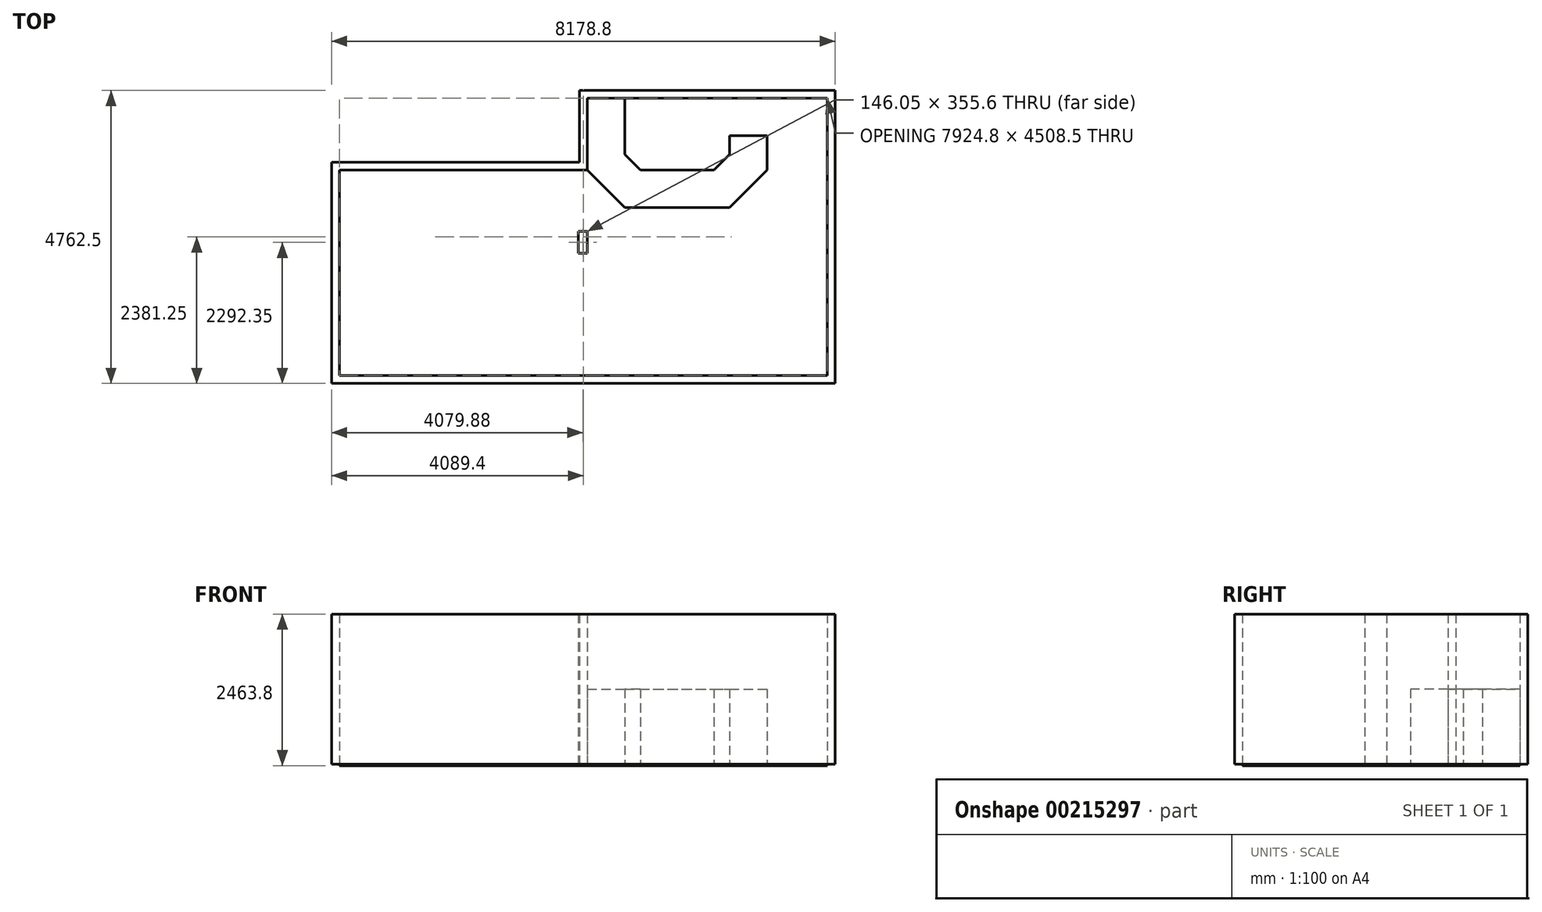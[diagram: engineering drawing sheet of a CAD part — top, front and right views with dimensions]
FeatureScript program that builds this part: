
annotation { "Feature Type Name" : "Feature", "Feature Type Description" : "" }
export const myFeature = defineFeature(function(context is Context, id is Id, definition is map)
    precondition{}
    {
        {
            var Q0;
            Q0=qCreatedBy(makeId("Top.planeOp"),FACE);
            var sketch = newSketch(context, id + "F0", { "sketchPlane" : qUnion([Q0])});
            skLineSegment(sketch, "E0.bottom", {"start": v(3962.4, 2254.25) * mm, "end": v(63.5, 2254.25) * mm});
            skLineSegment(sketch, "E0.top", {"start": v(3962.4, -2254.25) * mm, "end": v(-3962.4, -2254.25) * mm});
            skLineSegment(sketch, "E0.left", {"start": v(3962.4, 2254.25) * mm, "end": v(3962.4, -2254.25) * mm});
            skLineSegment(sketch, "E0.right", {"start": v(-3962.4, 1085.85) * mm, "end": v(-3962.4, -2254.25) * mm});
            skPoint(sketch, "E0.middle", {"position": v(0, 0) * mm});
            skLineSegment(sketch, "E1", {"start": v(63.5, 2254.25) * mm, "end": v(63.5, 1085.85) * mm});
            skLineSegment(sketch, "E2", {"start": v(63.5, 1085.85) * mm, "end": v(-3962.4, 1085.85) * mm});
            skLineSegment(sketch, "E3.bottom", {"start": v(63.5, 88.9) * mm, "end": v(-82.55, 88.9) * mm});
            skLineSegment(sketch, "E3.top", {"start": v(63.5, -266.7) * mm, "end": v(-82.55, -266.7) * mm});
            skLineSegment(sketch, "E3.left", {"start": v(63.5, 88.9) * mm, "end": v(63.5, -266.7) * mm});
            skLineSegment(sketch, "E3.right", {"start": v(-82.55, 88.9) * mm, "end": v(-82.55, -266.7) * mm});
            skPoint(sketch, "E4.orphan", {"position": v(-3962.4, 2254.25) * mm});
            skLineSegment(sketch, "E5", {"start": v(-63.5, 2381.25) * mm, "end": v(4089.4, 2381.25) * mm});
            skLineSegment(sketch, "E6", {"start": v(4089.4, 2381.25) * mm, "end": v(4089.4, -2381.25) * mm});
            skLineSegment(sketch, "E7", {"start": v(-4089.4, -2381.25) * mm, "end": v(4089.4, -2381.25) * mm});
            skLineSegment(sketch, "E8", {"start": v(-4089.4, -2381.25) * mm, "end": v(-4089.4, 1212.85) * mm});
            skLineSegment(sketch, "E9", {"start": v(-4089.4, 1212.85) * mm, "end": v(-63.5, 1212.85) * mm});
            skLineSegment(sketch, "E10", {"start": v(-63.5, 1212.85) * mm, "end": v(-63.5, 2381.25) * mm});
            skSolve(sketch);
        }
        {
            var Q0;
            Q0=makeQuery(id+"F0.imprint","IMPRINT",FACE,{"disambiguationData":[TD([[makeQuery(id+"F0.imprint","IMPRINT",EDGE,{"derivedFrom":sQuery(id+"F0.wireOp",EDGE,"E0.bottom")}),-1.0]])]});
            extrude(context, id + "F1", {"entities" : qUnion([Q0]), "depth" : 2438.4 * mm});
        }
        {
            var Q0;
            Q0=makeQuery(id+"F0.imprint","IMPRINT",FACE,{"disambiguationData":[TD([[makeQuery(id+"F0.imprint","IMPRINT",EDGE,{"derivedFrom":sQuery(id+"F0.wireOp",EDGE,"E0.bottom")}),1.0]])]});
            extrude(context, id + "F2", {"entities" : qUnion([Q0]), "operationType" : NewBodyOperationType.ADD, "oppositeDirection" : true, "depth" : 25.4 * mm});
        }
        {
            var Q0;
            Q0=makeQuery(id+"F0.imprint","IMPRINT",FACE,{"disambiguationData":[TD([[makeQuery(id+"F0.imprint","IMPRINT",EDGE,{"derivedFrom":sQuery(id+"F0.wireOp",EDGE,"E3.bottom")}),1.0]])]});
            extrude(context, id + "F3", {"entities" : qUnion([Q0]), "depth" : 2438.4 * mm});
        }
        {
            var Q0;
            Q0=makeQuery(id+"F0.imprint","IMPRINT",FACE,{"disambiguationData":[TD([[makeQuery(id+"F0.imprint","IMPRINT",EDGE,{"derivedFrom":sQuery(id+"F0.wireOp",EDGE,"E0.bottom")}),1.0]])]});
            var sketch = newSketch(context, id + "F4", { "sketchPlane" : qUnion([Q0])});
            skPoint(sketch, "E11.0", {"position": v(63.5, 1085.85) * mm});
            skLineSegment(sketch, "E12", {"start": v(63.5, 1085.85) * mm, "end": v(673.1, 476.25) * mm});
            skLineSegment(sketch, "E13", {"start": v(673.1, 476.25) * mm, "end": v(2374.9, 476.25) * mm});
            skLineSegment(sketch, "E14", {"start": v(2374.9, 476.25) * mm, "end": v(2984.5, 1085.85) * mm});
            skLineSegment(sketch, "E15", {"start": v(2984.5, 1644.65) * mm, "end": v(2984.5, 1085.85) * mm});
            skLineSegment(sketch, "E16", {"start": v(925.6, 1085.85) * mm, "end": v(2122.4, 1085.85) * mm});
            skLineSegment(sketch, "E17", {"start": v(2122.4, 1085.85) * mm, "end": v(2374.9, 1338.35) * mm});
            skLineSegment(sketch, "E18", {"start": v(2374.9, 1338.35) * mm, "end": v(2374.9, 1644.65) * mm});
            skLineSegment(sketch, "E19", {"start": v(2374.9, 1644.65) * mm, "end": v(2984.5, 1644.65) * mm});
            skLineSegment(sketch, "E20", {"start": v(673.1, 1338.35) * mm, "end": v(673.1, 2254.25) * mm});
            skLineSegment(sketch, "E21.0", {"start": v(63.5, 2254.25) * mm, "end": v(63.5, 1085.85) * mm});
            skLineSegment(sketch, "E22", {"start": v(673.1, 2254.25) * mm, "end": v(63.5, 2254.25) * mm});
            skLineSegment(sketch, "E23", {"start": v(63.5, 1085.85) * mm, "end": v(63.5, 2254.25) * mm});
            skLineSegment(sketch, "E24", {"start": v(925.6, 1085.85) * mm, "end": v(673.1, 1338.35) * mm});
            skSolve(sketch);
        }
        {
            var Q0;
            Q0=makeQuery(id+"F4.imprint","IMPRINT",FACE,{"disambiguationData":[TD([[makeQuery(id+"F4.imprint","IMPRINT",EDGE,{"derivedFrom":sQuery(id+"F4.wireOp",EDGE,"E12")}),1.0]])]});
            extrude(context, id + "F5", {"entities" : qUnion([Q0]), "depth" : 1219.2 * mm});
        }
    });
